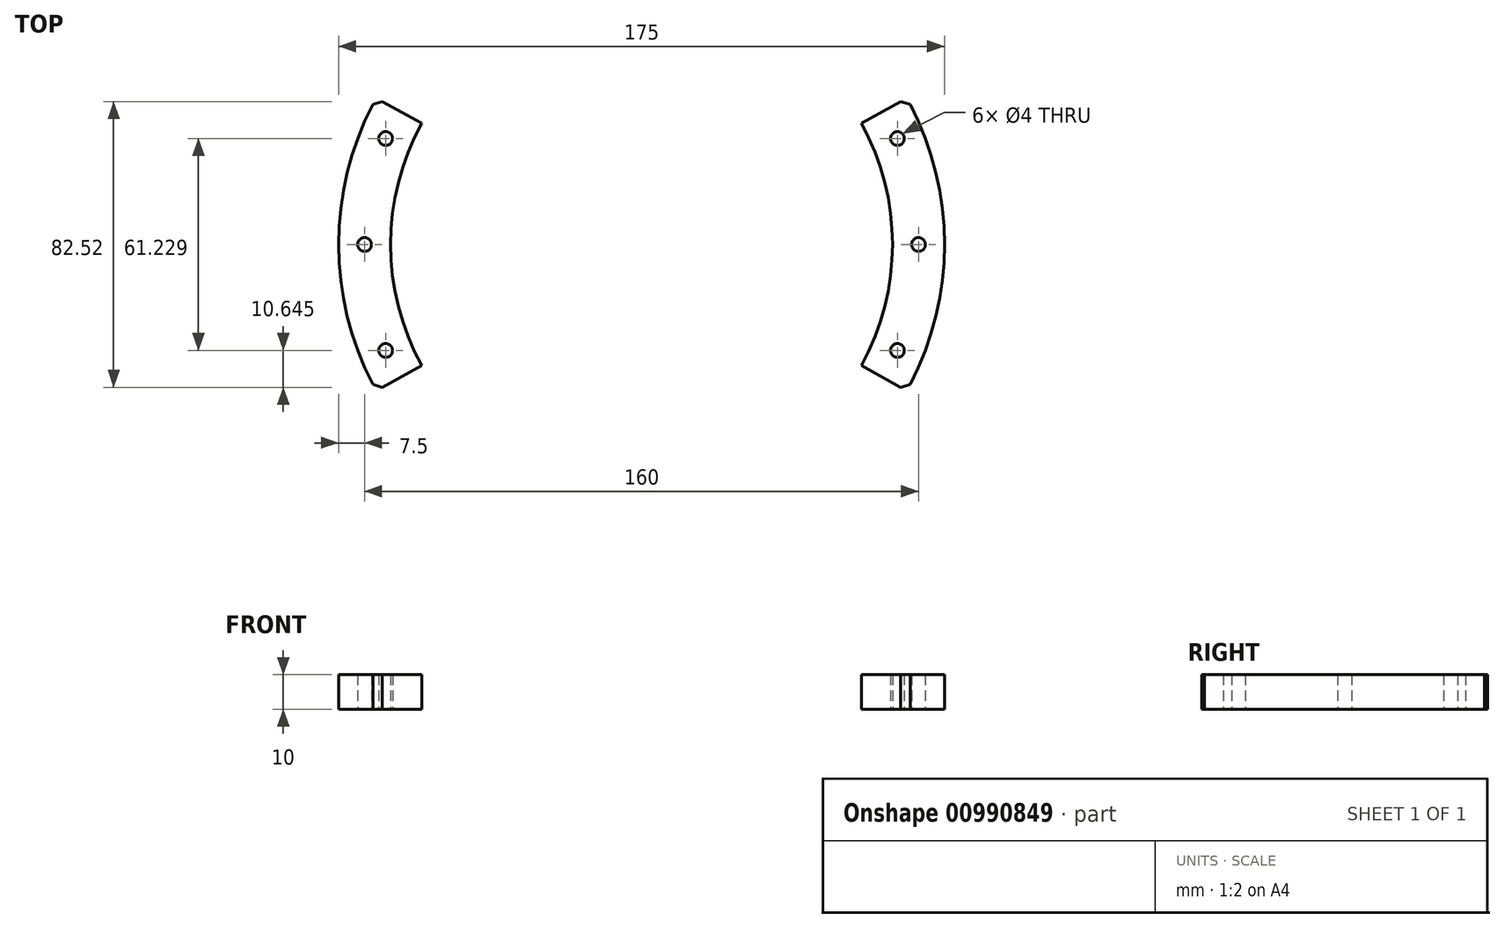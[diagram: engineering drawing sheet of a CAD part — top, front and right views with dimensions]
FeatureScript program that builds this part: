
annotation { "Feature Type Name" : "Feature", "Feature Type Description" : "" }
export const myFeature = defineFeature(function(context is Context, id is Id, definition is map)
    precondition{}
    {
        {
            var Q0;
            Q0=qCreatedBy(makeId("Top.planeOp"),FACE);
            var sketch = newSketch(context, id + "F0", { "sketchPlane" : qUnion([Q0])});
            skArc(sketch, "E0", {"start": v(-55.64, 25) * mm, "mid": v(-61, 0) * mm, "end": v(-55.64, -25) * mm});
            skArc(sketch, "E1.trimOffspring", {"start": v(55.64, -25) * mm, "mid": v(61, 0) * mm, "end": v(55.64, 25) * mm});
            skCircle(sketch, "E2", {"center": v(0, 0) * mm, "radius": 61 * mm});
            skCircle(sketch, "E3", {"center": v(0, 0) * mm, "radius": 72.5 * mm});
            skLineSegment(sketch, "E4", {"start": v(-63.5, 35) * mm, "end": v(-63.5, -35) * mm, "construction": true});
            skCircle(sketch, "E5", {"center": v(0, 0) * mm, "radius": 87.5 * mm});
            skLineSegment(sketch, "E6", {"start": v(-63.5, 35) * mm, "end": v(-76.63, 42.24) * mm});
            skLineSegment(sketch, "E7", {"start": v(-63.5, -35) * mm, "end": v(-76.63, -42.24) * mm});
            skArc(sketch, "E8", {"start": v(-70.06, -38.62) * mm, "mid": v(-80, 0) * mm, "end": v(-70.06, 38.62) * mm, "construction": true});
            skCircle(sketch, "E9", {"center": v(-80, 0) * mm, "radius": 2 * mm});
            skCircle(sketch, "E10.1.0", {"center": v(-73.91, -30.61) * mm, "radius": 2 * mm});
            skCircle(sketch, "E10.2.0", {"center": v(-56.57, -56.57) * mm, "radius": 2 * mm});
            skCircle(sketch, "E11.1.3.0", {"center": v(-30.61, -73.91) * mm, "radius": 2 * mm});
            skCircle(sketch, "E11.1.4.0", {"center": v(0, -80) * mm, "radius": 2 * mm});
            skCircle(sketch, "E11.1.5.0", {"center": v(30.61, -73.91) * mm, "radius": 2 * mm});
            skCircle(sketch, "E11.1.6.0", {"center": v(56.57, -56.57) * mm, "radius": 2 * mm});
            skCircle(sketch, "E11.1.7.0", {"center": v(73.91, -30.61) * mm, "radius": 2 * mm});
            skCircle(sketch, "E12.1.8.0", {"center": v(80, 0) * mm, "radius": 2 * mm});
            skCircle(sketch, "E12.1.9.0", {"center": v(73.91, 30.61) * mm, "radius": 2 * mm});
            skCircle(sketch, "E12.1.10.0", {"center": v(56.57, 56.57) * mm, "radius": 2 * mm});
            skCircle(sketch, "E12.1.11.0", {"center": v(30.61, 73.91) * mm, "radius": 2 * mm});
            skCircle(sketch, "E13.1.12.0", {"center": v(0, 80) * mm, "radius": 2 * mm});
            skCircle(sketch, "E13.1.13.0", {"center": v(-30.61, 73.91) * mm, "radius": 2 * mm});
            skCircle(sketch, "E13.1.14.0", {"center": v(-56.57, 56.57) * mm, "radius": 2 * mm});
            skCircle(sketch, "E13.1.15.0", {"center": v(-73.91, 30.61) * mm, "radius": 2 * mm});
            skLineSegment(sketch, "E14", {"start": v(-63.5, 35) * mm, "end": v(-49.96, 35) * mm});
            skLineSegment(sketch, "E15", {"start": v(-63.5, -35) * mm, "end": v(-49.96, -35) * mm});
            skSolve(sketch);
        }
        {
            var Q0;
            {var subQ1=sQuery(id+"F0.wireOp",EDGE,"E8");var subQ8=sQuery(id+"F0.wireOp",EDGE,"E7");var subQ22=makeQuery(id+"F0.imprint","INTERSECT",VERTEX,{"derivedFrom":[subQ8,subQ1]});Q0=makeQuery(id+"F0.imprint","IMPRINT",FACE,{"disambiguationData":[TD([[makeQuery(id+"F0.imprint","IMPRINT",EDGE,{"disambiguationData":[TD([[subQ22,-1.0]])],"derivedFrom":subQ1}),-1.0]])]});}
            var Q1;
            {var subQ11=sQuery(id+"F0.wireOp",EDGE,"E6");var subQ12=sQuery(id+"F0.wireOp",EDGE,"E5");var subQ13=makeQuery(id+"F0.imprint","INTERSECT",VERTEX,{"derivedFrom":[subQ12,subQ11]});Q1=makeQuery(id+"F0.imprint","IMPRINT",FACE,{"disambiguationData":[TD([[makeQuery(id+"F0.imprint","IMPRINT",EDGE,{"disambiguationData":[TD([[subQ13,-1.0]])],"derivedFrom":subQ12}),1.0]])]});}
            extrude(context, id + "F1", {"entities" : qUnion([Q0, Q1]), "depth" : 10 * mm, "offsetDistance" : 25 * mm});
        }
        {
            var Q0;
            Q0=makeQuery(id+"F1.opExtrude","SWEPT_EDGE",EDGE,{"disambiguationData":[OSD([sQuery(id+"F0.wireOp",EDGE,"E5"),sQuery(id+"F0.wireOp",EDGE,"E6")])]});
            var Q1;
            Q1=makeQuery(id+"F1.opExtrude","SWEPT_EDGE",EDGE,{"disambiguationData":[OSD([sQuery(id+"F0.wireOp",EDGE,"E5"),sQuery(id+"F0.wireOp",EDGE,"E7")])]});
            chamfer(context, id + "F2", {"entities" : qUnion([Q0, Q1]), "width" : 2 * mm, "tangentPropagation" : true});
        }
        {
            var Q0;
            Q0=makeQuery(id+"F1.opExtrude","SWEPT_BODY",BODY,{"disambiguationData":[OSD([sQuery(id+"F0.wireOp",EDGE,"E3"),sQuery(id+"F0.wireOp",EDGE,"E5"),sQuery(id+"F0.wireOp",EDGE,"E6"),sQuery(id+"F0.wireOp",EDGE,"E7"),sQuery(id+"F0.wireOp",EDGE,"E9"),sQuery(id+"F0.wireOp",EDGE,"E10.1.0"),sQuery(id+"F0.wireOp",EDGE,"E13.1.15.0")])]});
            var Q1;
            Q1=qCreatedBy(makeId("Right.planeOp"),FACE);
            mirror(context, id + "F3", {"entities" : qUnion([Q0]), "mirrorPlane" : qUnion([Q1])});
        }
    });
